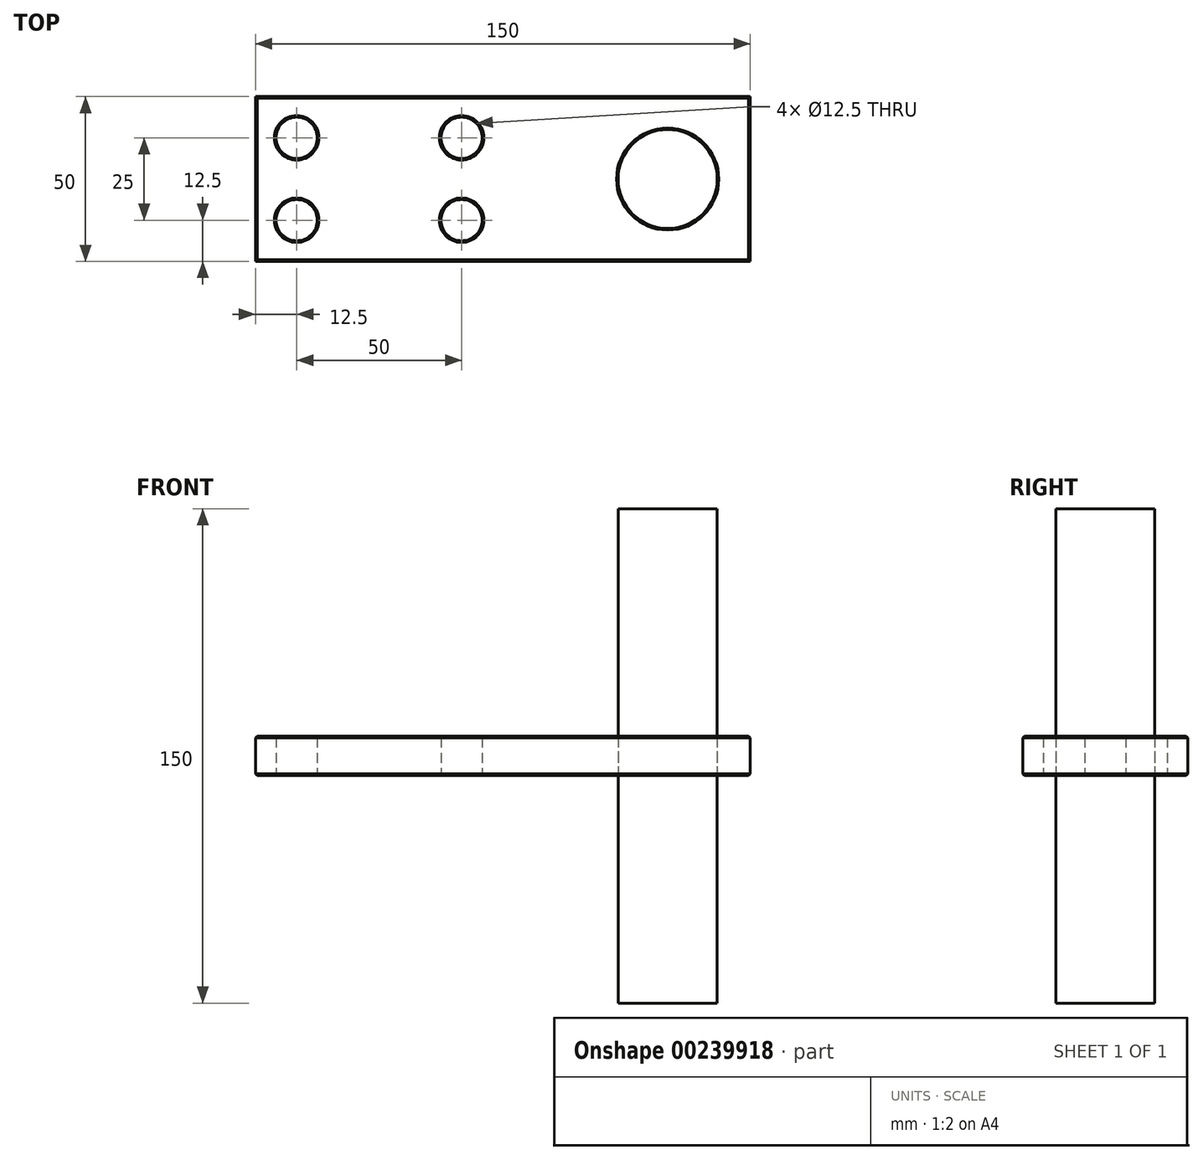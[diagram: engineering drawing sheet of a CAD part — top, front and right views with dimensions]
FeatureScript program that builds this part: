
annotation { "Feature Type Name" : "Feature", "Feature Type Description" : "" }
export const myFeature = defineFeature(function(context is Context, id is Id, definition is map)
    precondition{}
    {
        {
            var Q0;
            Q0=qCreatedBy(makeId("Top.planeOp"),FACE);
            var sketch = newSketch(context, id + "F0", { "sketchPlane" : qUnion([Q0])});
            skLineSegment(sketch, "E0.bottom", {"start": v(75, -25) * mm, "end": v(-75, -25) * mm});
            skLineSegment(sketch, "E0.top", {"start": v(75, 25) * mm, "end": v(-75, 25) * mm});
            skLineSegment(sketch, "E0.left", {"start": v(75, -25) * mm, "end": v(75, 25) * mm});
            skLineSegment(sketch, "E0.right", {"start": v(-75, -25) * mm, "end": v(-75, 25) * mm});
            skPoint(sketch, "E0.middle", {"position": v(0, 0) * mm});
            skLineSegment(sketch, "E1", {"start": v(0, 0) * mm, "end": v(-75, 0) * mm, "construction": true});
            skLineSegment(sketch, "E2.0", {"start": v(0, 12.5) * mm, "end": v(-75, 12.5) * mm, "construction": true});
            skLineSegment(sketch, "E3.0", {"start": v(0, -12.5) * mm, "end": v(-75, -12.5) * mm, "construction": true});
            skLineSegment(sketch, "E4.0", {"start": v(-62.5, -25) * mm, "end": v(-62.5, 25) * mm, "construction": true});
            skLineSegment(sketch, "E5.0", {"start": v(-12.5, -25) * mm, "end": v(-12.5, 25) * mm, "construction": true});
            skCircle(sketch, "E6", {"center": v(-62.5, 12.5) * mm, "radius": 6.25 * mm});
            skCircle(sketch, "E7", {"center": v(-12.5, 12.5) * mm, "radius": 6.25 * mm});
            skCircle(sketch, "E8", {"center": v(-12.5, -12.5) * mm, "radius": 6.25 * mm});
            skCircle(sketch, "E9", {"center": v(-62.5, -12.5) * mm, "radius": 6.25 * mm});
            skLineSegment(sketch, "E10", {"start": v(0, 0) * mm, "end": v(50, 0) * mm, "construction": true});
            skCircle(sketch, "E11", {"center": v(50, 0) * mm, "radius": 15 * mm});
            skSolve(sketch);
        }
        {
            var Q0;
            Q0=makeQuery(id+"F0.imprint","IMPRINT",FACE,{"disambiguationData":[TD([[makeQuery(id+"F0.imprint","IMPRINT",EDGE,{"derivedFrom":sQuery(id+"F0.wireOp",EDGE,"E0.bottom")}),-1.0]])]});
            extrude(context, id + "F1", {"entities" : qUnion([Q0]), "endBound" : BoundingType.SYMMETRIC, "depth" : 12 * mm});
        }
        {
            var Q0;
            Q0=makeQuery(id+"F1.opExtrude","CAP_FACE",FACE,{"disambiguationData":[OSD([sQuery(id+"F0.wireOp",EDGE,"E0.bottom"),sQuery(id+"F0.wireOp",EDGE,"E0.top"),sQuery(id+"F0.wireOp",EDGE,"E0.left"),sQuery(id+"F0.wireOp",EDGE,"E0.right"),sQuery(id+"F0.wireOp",EDGE,"E6"),sQuery(id+"F0.wireOp",EDGE,"E7"),sQuery(id+"F0.wireOp",EDGE,"E8"),sQuery(id+"F0.wireOp",EDGE,"E9"),sQuery(id+"F0.wireOp",EDGE,"E11")])],"isStart":false});
            var Q1;
            Q1=makeQuery(id+"F1.opExtrude","CAP_FACE",FACE,{"disambiguationData":[OSD([sQuery(id+"F0.wireOp",EDGE,"E0.bottom"),sQuery(id+"F0.wireOp",EDGE,"E0.top"),sQuery(id+"F0.wireOp",EDGE,"E0.left"),sQuery(id+"F0.wireOp",EDGE,"E0.right"),sQuery(id+"F0.wireOp",EDGE,"E6"),sQuery(id+"F0.wireOp",EDGE,"E7"),sQuery(id+"F0.wireOp",EDGE,"E8"),sQuery(id+"F0.wireOp",EDGE,"E9"),sQuery(id+"F0.wireOp",EDGE,"E11")])],"isStart":true});
            chamfer(context, id + "F2", {"entities" : qUnion([Q0, Q1]), "width" : .5 * mm, "tangentPropagation" : true});
        }
        {
            var Q0;
            Q0=makeQuery(id+"F0.imprint","IMPRINT",FACE,{"disambiguationData":[TD([[makeQuery(id+"F0.imprint","IMPRINT",EDGE,{"derivedFrom":sQuery(id+"F0.wireOp",EDGE,"E11")}),1.0]])]});
            extrude(context, id + "F3", {"entities" : qUnion([Q0]), "endBound" : BoundingType.SYMMETRIC, "depth" : 150 * mm});
        }
    });
